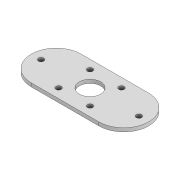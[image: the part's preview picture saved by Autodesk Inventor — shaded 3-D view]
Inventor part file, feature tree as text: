
AUTODESK INVENTOR PART (.ipt)
format: ipt  version: 2022 (Build 260153000, 153)  size: 135,680 bytes
history: native  units: mm
features: extrude x1, sketch x1, projected_geometry x1
ambient origin geometry x8: Origin, YZ Plane, XZ Plane, XY Plane, X Axis, Y Axis, Z Axis, Center Point
bodies: Body1 (feature_tree)
feature tree (3):
  extrude  "Extrusion2"  Depth=28.0mm
  sketch  "Sketch3"  dims[d37=3.0mm d38=3.0mm d39=3.0mm d40=3.0mm d41=12.5mm d42=12.5mm d43=12.5mm d44=12.5mm d55=2.0mm d56=0.0mm d60=28.0mm d61=12.0mm d66=5.0mm d67=5.0mm d68=3.0mm d69=3.0mm d70=8.5mm d71=8.5mm]
  projected_geometry  "Projected Loop1"
